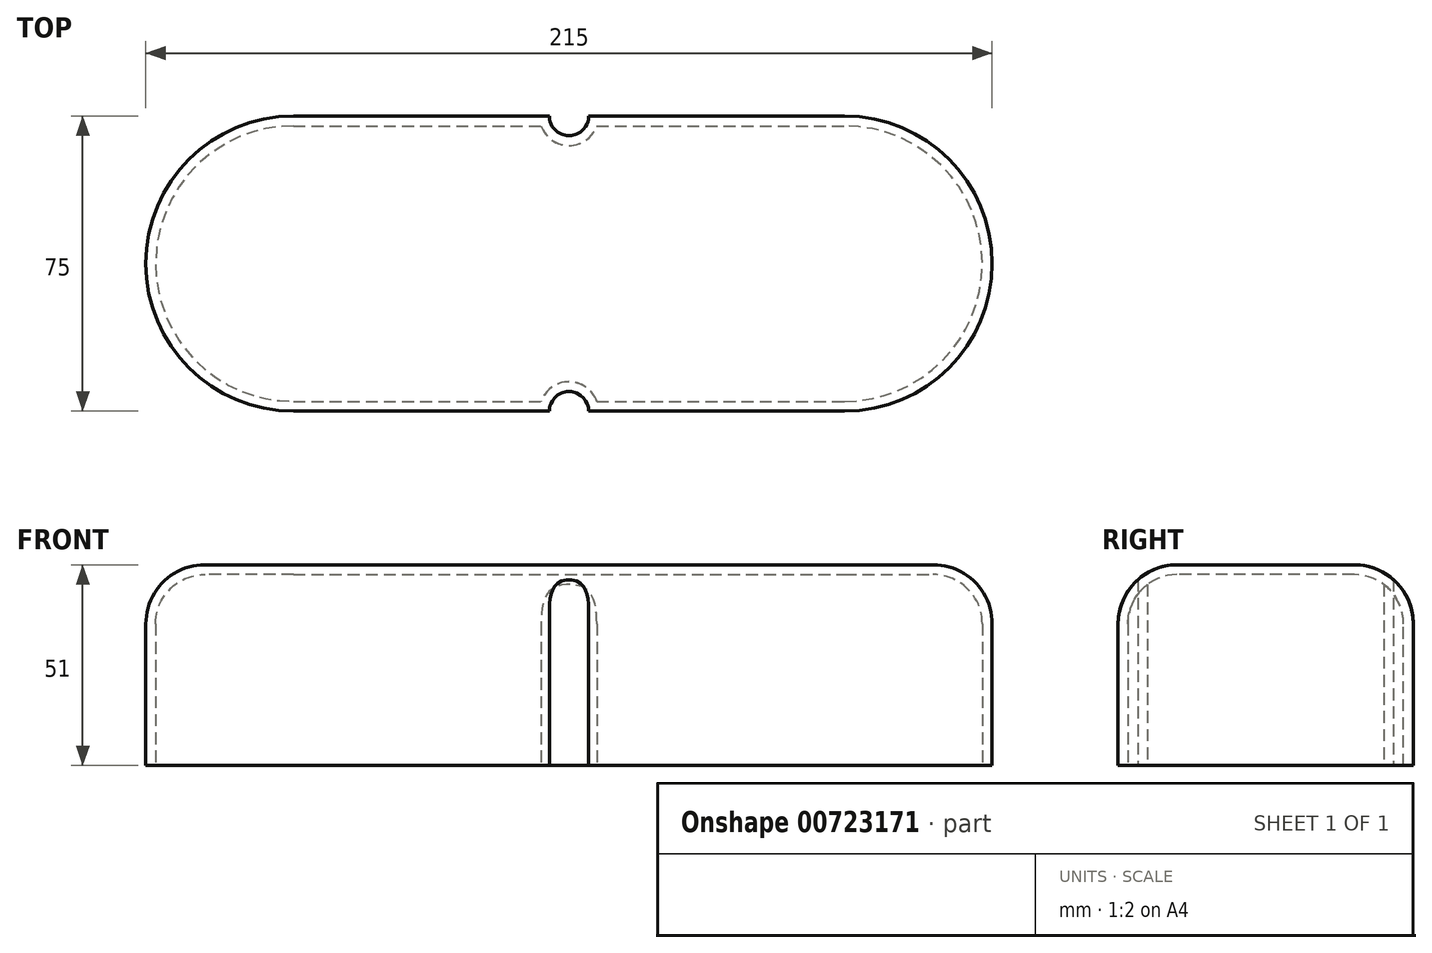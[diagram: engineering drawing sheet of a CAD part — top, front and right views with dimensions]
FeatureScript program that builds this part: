
annotation { "Feature Type Name" : "Feature", "Feature Type Description" : "" }
export const myFeature = defineFeature(function(context is Context, id is Id, definition is map)
    precondition{}
    {
        {
            var Q0;
            Q0=qCreatedBy(makeId("Top.planeOp"),FACE);
            var sketch = newSketch(context, id + "F0", { "sketchPlane" : qUnion([Q0])});
            skLineSegment(sketch, "E0.bottom", {"start": v(-70, -37.5) * mm, "end": v(70, -37.5) * mm});
            skLineSegment(sketch, "E0.top", {"start": v(-70, 37.5) * mm, "end": v(70, 37.5) * mm});
            skLineSegment(sketch, "E0.left", {"start": v(-70, -37.5) * mm, "end": v(-70, 37.5) * mm});
            skLineSegment(sketch, "E0.right", {"start": v(70, -37.5) * mm, "end": v(70, 37.5) * mm});
            skPoint(sketch, "E0.middle", {"position": v(0, 0) * mm});
            skArc(sketch, "E1", {"start": v(-70, 37.5) * mm, "mid": v(-107.5, 0) * mm, "end": v(-70, -37.5) * mm});
            skArc(sketch, "E2", {"start": v(70, -37.5) * mm, "mid": v(107.5, 0) * mm, "end": v(70, 37.5) * mm});
            skLineSegment(sketch, "E3", {"start": v(0, 0) * mm, "end": v(0, -37.5) * mm});
            skLineSegment(sketch, "E4", {"start": v(0, 0) * mm, "end": v(0, 37.5) * mm});
            skArc(sketch, "E5", {"start": v(5, 37.5) * mm, "mid": v(0, 32.5) * mm, "end": v(-5, 37.5) * mm});
            skArc(sketch, "E6", {"start": v(-5, -37.5) * mm, "mid": v(0, -32.5) * mm, "end": v(5, -37.5) * mm});
            skSolve(sketch);
        }
        {
            var Q0;
            {var subQ5=sQuery(id+"F0.wireOp",EDGE,"E0.left");Q0=makeQuery(id+"F0.imprint","IMPRINT",FACE,{"disambiguationData":[TD([[makeQuery(id+"F0.imprint","IMPRINT",EDGE,{"derivedFrom":subQ5}),-1.0]])]});}
            var Q1;
            Q1=makeQuery(id+"F0.imprint","IMPRINT",FACE,{"disambiguationData":[TD([[makeQuery(id+"F0.imprint","IMPRINT",EDGE,{"derivedFrom":sQuery(id+"F0.wireOp",EDGE,"E0.left")}),1.0]])]});
            var Q2;
            {var subQ0=sQuery(id+"F0.wireOp",EDGE,"E0.right");Q2=makeQuery(id+"F0.imprint","IMPRINT",FACE,{"disambiguationData":[TD([[makeQuery(id+"F0.imprint","IMPRINT",EDGE,{"derivedFrom":subQ0}),1.0]])]});}
            var Q3;
            Q3=makeQuery(id+"F0.imprint","IMPRINT",FACE,{"disambiguationData":[TD([[makeQuery(id+"F0.imprint","IMPRINT",EDGE,{"derivedFrom":sQuery(id+"F0.wireOp",EDGE,"E0.right")}),-1.0]])]});
            extrude(context, id + "F1", {"entities" : qUnion([Q0, Q1, Q2, Q3]), "depth" : 51 * mm, "offsetDistance" : 25 * mm});
        }
        {
            var Q0;
            {var subQ0=sQuery(id+"F0.wireOp",EDGE,"E0.bottom");Q0=makeQuery(id+"F1.opExtrude","CAP_EDGE",EDGE,{"disambiguationData":[OSD([subQ0]),TDD([makeQuery(id+"F0.imprint","IMPRINT",EDGE,{"disambiguationData":[TD([[makeQuery(id+"F0.imprint","INTERSECT",VERTEX,{"disambiguationData":[OD(1.0)],"derivedFrom":[subQ0,sQuery(id+"F0.wireOp",EDGE,"E6")]}),-1.0]])],"derivedFrom":subQ0})])],"isStart":false});}
            var Q1;
            Q1=makeQuery(id+"F1.opExtrude","CAP_EDGE",EDGE,{"disambiguationData":[OSD([sQuery(id+"F0.wireOp",EDGE,"E2")])],"isStart":false});
            var Q2;
            {var subQ0=sQuery(id+"F0.wireOp",EDGE,"E0.top");Q2=makeQuery(id+"F1.opExtrude","CAP_EDGE",EDGE,{"disambiguationData":[OSD([subQ0]),TDD([makeQuery(id+"F0.imprint","IMPRINT",EDGE,{"disambiguationData":[TD([[makeQuery(id+"F0.imprint","INTERSECT",VERTEX,{"disambiguationData":[OD(1.0)],"derivedFrom":[subQ0,sQuery(id+"F0.wireOp",EDGE,"E5")]}),1.0]])],"derivedFrom":subQ0})])],"isStart":false});}
            fillet(context, id + "F2", {"entities" : qUnion([Q0, Q1, Q2]), "radius" : 15 * mm, "tangentPropagation" : true, "allowEdgeOverflow" : false});
        }
        {
            var Q0;
            Q0=makeQuery(id+"F1.opExtrude","CAP_FACE",FACE,{"disambiguationData":[OSD([sQuery(id+"F0.wireOp",EDGE,"E0.bottom"),sQuery(id+"F0.wireOp",EDGE,"E0.top"),sQuery(id+"F0.wireOp",EDGE,"E1"),sQuery(id+"F0.wireOp",EDGE,"E2"),sQuery(id+"F0.wireOp",EDGE,"E5"),sQuery(id+"F0.wireOp",EDGE,"E6")])],"isStart":true});
            shell(context, id + "F3", {"entities" : qUnion([Q0]), "thickness" : 2.5 * mm});
        }
    });
